# Revit family: Combination-Metcraft-Patient Care-9610R
name_source: partatom
category: Plumbing Fixtures
revit_build: Autodesk Revit MEP 2015 (Build: 20140606_1530(x64)
units: mm (PartAtom-declared; Revit-internal decimal feet)

## types (1)
- Hide-A-Way Patient Care Fixture
    ADA Compliant = N.A.
    Assembly Code = D2010100
    CW Connection = Yes
    Countertop = Laminated Formica, WilsonArt, or Nevamar
    Description = Hide-A-Way Patient Care Fixture
    Fixture Hyperlink = http://metcraftindustries.com
    Fixture Submittal = http://metcraftindustries.com
    Flushvalve Connection = 1"
    HW Connection = Yes
    Industry Standards = ASME A112.19.3 / CSA B45.4
    Instalation Type = Wall Outlet Waste
    Lav Waste Tube = 1.5"
    Lav. C.W. Connection = .5"
    Lav. H.W. Connection = .5"
    Manufacturer = Metcraft Industries
    Manufacturer URL = http://metcraftindustries.com
    MasterFormat Title = Healthcare Plumbing Fixture
    Masterformat Number = 22 43 00
    Material = 304 Stainless Steel
    Model = 9610R
    Mounting Height = 0' - 0"
    Omniclass Number = 23-31 19 11
    Omniclass Title = Combination Toilets
    Waste Connection = Yes
    Waste Tube = 3"

## geometry (parser evidence)
native form markers: Sweep x4
no freeform markers — native parametric forms only
